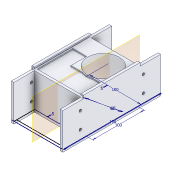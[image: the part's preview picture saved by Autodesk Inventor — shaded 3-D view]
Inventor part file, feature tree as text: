
AUTODESK INVENTOR PART (.ipt)
format: ipt  version: 2020.3 (Build 243373010, 373A)  size: 227,840 bytes
history: native  units: mm
features: extrude x10, sketch x7, hole x1, plane x1, mirror x1
ambient origin geometry x8: Origin, YZ Plane, XZ Plane, XY Plane, X Axis, Y Axis, Z Axis, Center Point
bodies: Solid1 (feature_tree)
feature tree (20):
  sketch  "Sketch1"  dims[d0=190.0mm d1=100.0mm]
  extrude  "Extrusion1"  Depth=100.0mm
  extrude  "Extrusion2"  Depth=5.0mm
  extrude  "Extrusion3"  Depth=65.0mm TaperAngle=0.0deg
  extrude  "Extrusion5"  Depth=65.0mm TaperAngle=0.0deg
  sketch  "Sketch2"  dims[d2=100.0mm d3=5.0mm]
  extrude  "Extrusion4"  Depth=65.0mm
  extrude  "Extrusion6"  Depth=65.0mm TaperAngle=0.0deg
  extrude  "Extrusion7"  Depth=10.0mm TaperAngle=0.0deg
  extrude  "Extrusion8"  Depth=10.0mm TaperAngle=0.0deg
  hole  "Hole1"  [1 undecoded]
  plane  "Work Plane1"
  mirror  "Mirror1"
  extrude  "Extrusion9"  Depth=10.0mm
  extrude  "Extrusion10"  Depth=10.0mm
  sketch  "Sketch3"  dims[d4=5.0mm d5=65.0mm d6=0.0mm]
  sketch  "Sketch4"  dims[d7=5.0mm d8=0.0mm d9=65.0mm d10=0.0mm]
  sketch  "Sketch5"  dims[d11=61.0mm d12=65.0mm]
  sketch  "Sketch6"  dims[d13=65.0mm d14=0.0mm d15=65.0mm d16=0.0mm]
  sketch  "Sketch7"  dims[d17=3.0mm d18=92.0mm d19=0.0mm d20=66.5mm d21=0.0mm d22=2.0mm d23=0.0mm d24=16.723mm d25=32.0mm d26=4.917mm d27=12.0mm d28=4.0mm d29=2.0mm d30=90.0deg d31=17.1mm d32=0.0mm d33=6.0mm d34=0.0mm d35=4.0mm d36=3.0mm d37=3.0mm d38=4.0mm d39=0.0mm d40=0.0mm d41=10.0mm d42=0.0mm]
note: 1 required parameter value undecoded (feature->parameter linkage not recoverable at this tier; creation-order binding heuristic only, values carry confidence <= 0.55)
